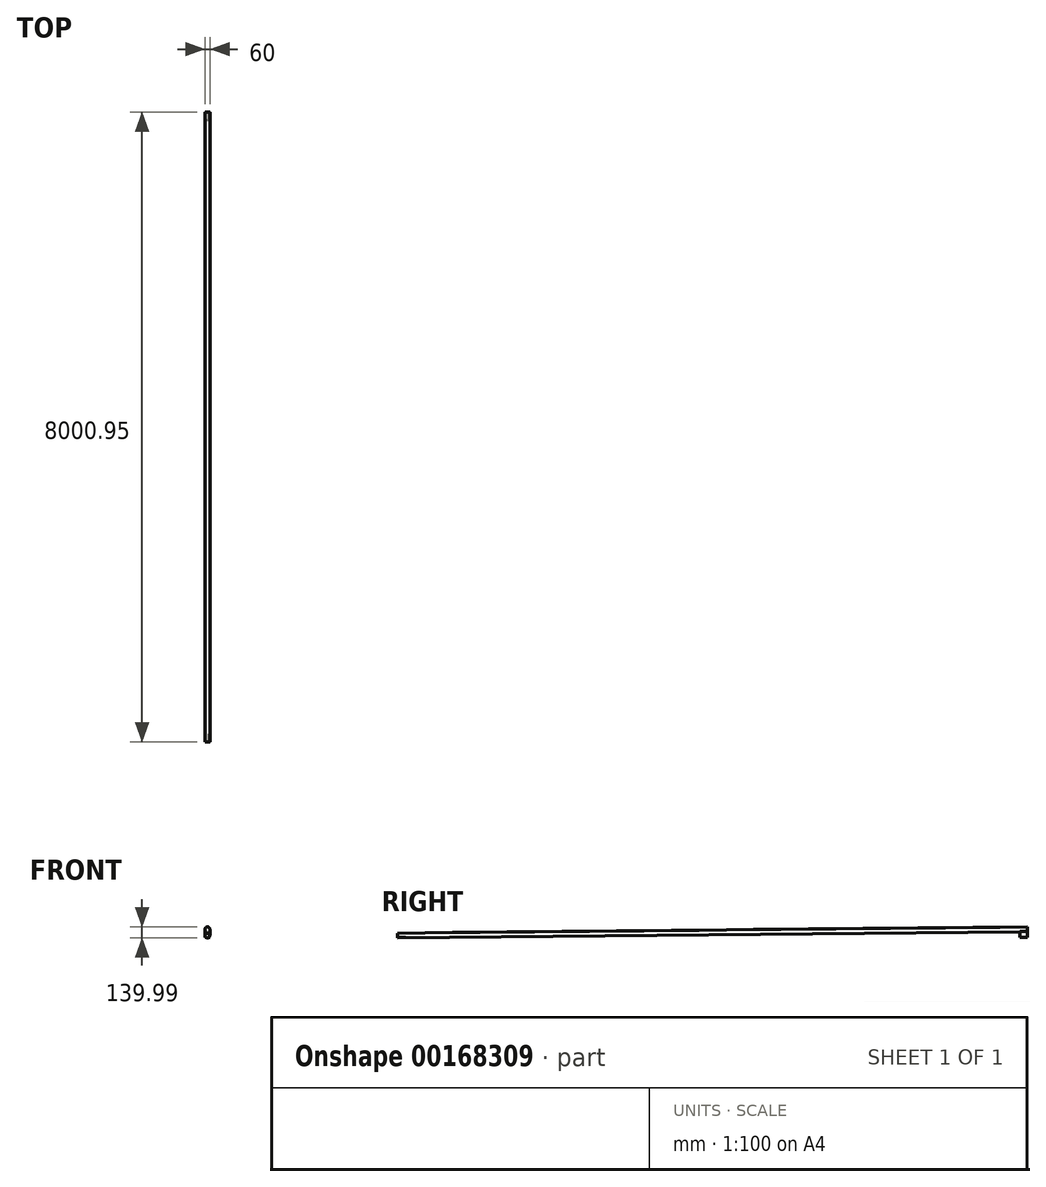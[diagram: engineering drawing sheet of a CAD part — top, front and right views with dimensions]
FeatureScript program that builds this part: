
annotation { "Feature Type Name" : "Feature", "Feature Type Description" : "" }
export const myFeature = defineFeature(function(context is Context, id is Id, definition is map)
    precondition{}
    {
        {
            var Q0;
            Q0=qCreatedBy(makeId("Right.planeOp"),FACE);
            var sketch = newSketch(context, id + "F0", { "sketchPlane" : qUnion([Q0])});
            skLineSegment(sketch, "E0", {"start": v(0, 0) * mm, "end": v(100, 1) * mm});
            skLineSegment(sketch, "E1", {"start": v(100, 1) * mm, "end": v(100, 0) * mm});
            skLineSegment(sketch, "E2", {"start": v(100, 0) * mm, "end": v(0, 0) * mm});
            skLineSegment(sketch, "E3", {"start": v(7900, 79) * mm, "end": v(7999.2, 80) * mm});
            skLineSegment(sketch, "E4", {"start": v(7999.2, 80) * mm, "end": v(8000, 0) * mm});
            skLineSegment(sketch, "E5", {"start": v(8000, 0) * mm, "end": v(7900, 0) * mm});
            skLineSegment(sketch, "E6", {"start": v(7900, 0) * mm, "end": v(7900, 79) * mm});
            skSolve(sketch);
        }
        {
            var Q0;
            Q0 = qSketchRegion(id + "F0", true);
            extrude(context, id + "F1", {"entities" : qUnion([Q0]), "depth" : 60 * mm});
        }
        {
            var Q0;
            Q0=makeQuery(id+"F1.opExtrude","SWEPT_FACE",FACE,{"disambiguationData":[OSD([sQuery(id+"F0.wireOp",EDGE,"E4")])]});
            var sketch = newSketch(context, id + "F2", { "sketchPlane" : qUnion([Q0])});
            skCircle(sketch, "E7", {"center": v(-30, 25) * mm, "radius": 30 * mm});
            skSolve(sketch);
        }
        {
            var Q0;
            Q0 = qSketchRegion(id + "F2", true);
            extrude(context, id + "F3", {"entities" : qUnion([Q0]), "operationType" : NewBodyOperationType.ADD, "oppositeDirection" : true, "depth" : 8000 * mm});
        }
    });
